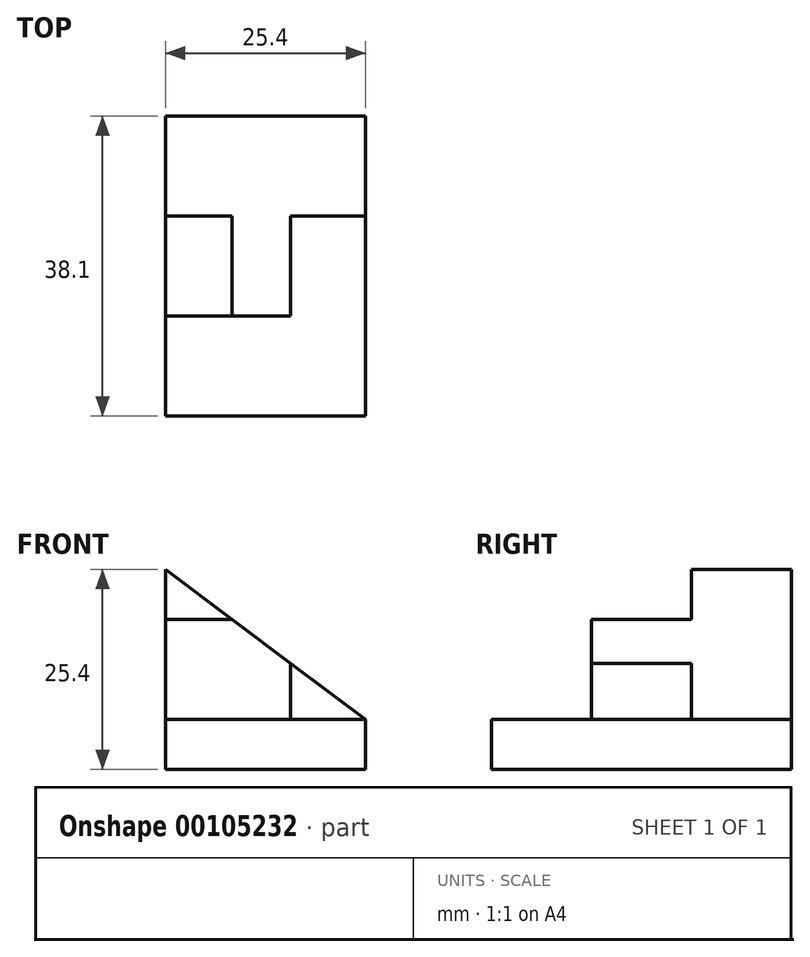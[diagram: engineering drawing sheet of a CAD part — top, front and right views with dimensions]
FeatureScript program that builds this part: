
annotation { "Feature Type Name" : "Feature", "Feature Type Description" : "" }
export const myFeature = defineFeature(function(context is Context, id is Id, definition is map)
    precondition{}
    {
        {
            var Q0;
            Q0=qCreatedBy(makeId("Front.planeOp"),FACE);
            var sketch = newSketch(context, id + "F0", { "sketchPlane" : qUnion([Q0])});
            skLineSegment(sketch, "E0.bottom", {"start": v(0, 0) * mm, "end": v(-25.4, 0) * mm});
            skLineSegment(sketch, "E0.top", {"start": v(0, 25.4) * mm, "end": v(-25.4, 25.4) * mm});
            skLineSegment(sketch, "E0.left", {"start": v(0, 0) * mm, "end": v(0, 25.4) * mm});
            skLineSegment(sketch, "E0.right", {"start": v(-25.4, 0) * mm, "end": v(-25.4, 25.4) * mm});
            skSolve(sketch);
        }
        {
            var Q0;
            Q0 = qSketchRegion(id + "F0", true);
            extrude(context, id + "F1", {"entities" : qUnion([Q0]), "endBound" : BoundingType.SYMMETRIC, "depth" : 38.1 * mm});
        }
        {
            var Q0;
            Q0=qCreatedBy(makeId("Front.planeOp"),FACE);
            var sketch = newSketch(context, id + "F2", { "sketchPlane" : qUnion([Q0])});
            skLineSegment(sketch, "E1", {"start": v(0, 6.35) * mm, "end": v(-25.4, 25.4) * mm});
            skLineSegment(sketch, "E2", {"start": v(-25.4, 25.4) * mm, "end": v(0, 25.4) * mm});
            skLineSegment(sketch, "E3", {"start": v(0, 6.35) * mm, "end": v(0, 25.4) * mm});
            skSolve(sketch);
        }
        {
            var Q0;
            Q0 = qSketchRegion(id + "F2", true);
            extrude(context, id + "F3", {"entities" : qUnion([Q0]), "operationType" : NewBodyOperationType.REMOVE, "endBound" : BoundingType.THROUGH_ALL, "oppositeDirection" : true, "depth" : 25.4 * mm, "hasSecondDirection" : true, "secondDirectionOppositeDirection" : false, "secondDirectionDepth" : 25.4 * mm});
        }
        {
            var Q0;
            Q0=qCreatedBy(makeId("Front.planeOp"),FACE);
            var sketch = newSketch(context, id + "F4", { "sketchPlane" : qUnion([Q0])});
            skLineSegment(sketch, "E4", {"start": v(-25.4, 19.05) * mm, "end": v(-16.93, 19.05) * mm});
            skLineSegment(sketch, "E5", {"start": v(-16.93, 19.05) * mm, "end": v(-25.4, 25.4) * mm});
            skLineSegment(sketch, "E6", {"start": v(-25.4, 25.4) * mm, "end": v(-25.4, 19.05) * mm});
            skSolve(sketch);
        }
        {
            var Q0;
            Q0 = qSketchRegion(id + "F4", true);
            extrude(context, id + "F5", {"entities" : qUnion([Q0]), "operationType" : NewBodyOperationType.REMOVE, "depth" : 25.4 * mm, "hasSecondDirection" : true, "secondDirectionOppositeDirection" : true, "secondDirectionDepth" : 6.35 * mm});
        }
        {
            var Q0;
            Q0=qCreatedBy(makeId("Right.planeOp"),FACE);
            var sketch = newSketch(context, id + "F6", { "sketchPlane" : qUnion([Q0])});
            skLineSegment(sketch, "E7.bottom", {"start": v(-6.35, 6.35) * mm, "end": v(-19.05, 6.35) * mm});
            skLineSegment(sketch, "E7.top", {"start": v(-6.35, 19.05) * mm, "end": v(-19.05, 19.05) * mm});
            skLineSegment(sketch, "E7.left", {"start": v(-6.35, 6.35) * mm, "end": v(-6.35, 19.05) * mm});
            skLineSegment(sketch, "E7.right", {"start": v(-19.05, 6.35) * mm, "end": v(-19.05, 19.05) * mm});
            skPoint(sketch, "E8.orphan", {"position": v(0, 6.35) * mm});
            skSolve(sketch);
        }
        {
            var Q0;
            Q0 = qSketchRegion(id + "F6", true);
            extrude(context, id + "F7", {"entities" : qUnion([Q0]), "operationType" : NewBodyOperationType.REMOVE, "endBound" : BoundingType.THROUGH_ALL, "oppositeDirection" : true, "depth" : 25.4 * mm});
        }
        {
            var Q0;
            Q0=qCreatedBy(makeId("Right.planeOp"),FACE);
            var sketch = newSketch(context, id + "F8", { "sketchPlane" : qUnion([Q0])});
            skLineSegment(sketch, "E9.bottom", {"start": v(0, 12.7) * mm, "end": v(6.35, 12.7) * mm});
            skLineSegment(sketch, "E9.top", {"start": v(0, 6.35) * mm, "end": v(6.35, 6.35) * mm});
            skLineSegment(sketch, "E9.left", {"start": v(0, 6.35) * mm, "end": v(0, 12.7) * mm});
            skLineSegment(sketch, "E9.right", {"start": v(6.35, 6.35) * mm, "end": v(6.35, 12.7) * mm});
            skSolve(sketch);
        }
        {
            var Q0;
            Q0 = qSketchRegion(id + "F8", true);
            extrude(context, id + "F9", {"entities" : qUnion([Q0]), "operationType" : NewBodyOperationType.REMOVE, "endBound" : BoundingType.SYMMETRIC, "oppositeDirection" : true, "depth" : 9.52 * mm});
        }
        {
            var Q0;
            Q0=qCreatedBy(makeId("Front.planeOp"),FACE);
            var sketch = newSketch(context, id + "F10", { "sketchPlane" : qUnion([Q0])});
            skLineSegment(sketch, "E10", {"start": v(-9.53, 13.5) * mm, "end": v(-9.53, 6.35) * mm});
            skLineSegment(sketch, "E11", {"start": v(-9.53, 6.35) * mm, "end": v(0, 6.35) * mm});
            skLineSegment(sketch, "E12", {"start": v(0, 6.35) * mm, "end": v(-9.52, 13.5) * mm});
            skSolve(sketch);
        }
        {
            var Q0;
            Q0 = qSketchRegion(id + "F10", true);
            extrude(context, id + "F11", {"entities" : qUnion([Q0]), "operationType" : NewBodyOperationType.REMOVE, "depth" : 25.4 * mm, "hasSecondDirection" : true, "secondDirectionOppositeDirection" : true, "secondDirectionDepth" : 6.35 * mm});
        }
    });
